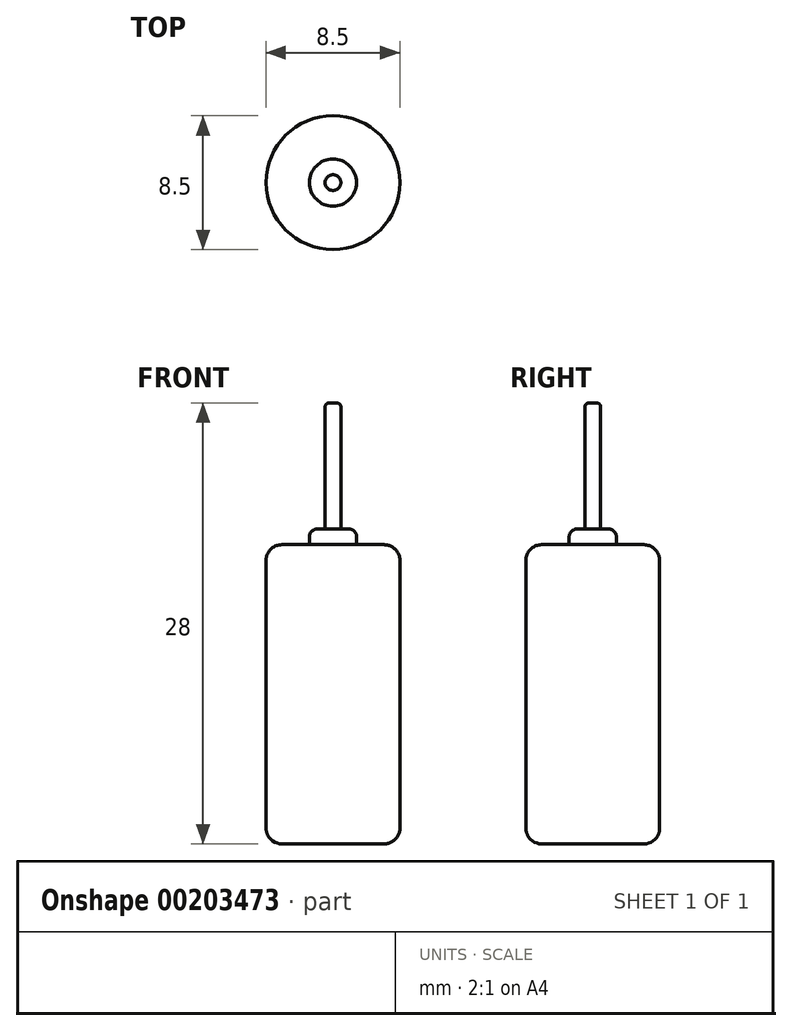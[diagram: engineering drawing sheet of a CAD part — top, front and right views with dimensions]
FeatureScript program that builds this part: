
annotation { "Feature Type Name" : "Feature", "Feature Type Description" : "" }
export const myFeature = defineFeature(function(context is Context, id is Id, definition is map)
    precondition{}
    {
        {
            var Q0;
            Q0=qCreatedBy(makeId("Top.planeOp"),FACE);
            var sketch = newSketch(context, id + "F0", { "sketchPlane" : qUnion([Q0])});
            skCircle(sketch, "E0", {"center": v(0, 0) * mm, "radius": 4.25 * mm});
            skSolve(sketch);
        }
        {
            var Q0;
            Q0=makeQuery(id+"F0.imprint","IMPRINT",FACE,{"disambiguationData":[TD([[makeQuery(id+"F0.imprint","IMPRINT",EDGE,{"derivedFrom":sQuery(id+"F0.wireOp",EDGE,"E0")}),1.0]])]});
            extrude(context, id + "F1", {"entities" : qUnion([Q0]), "depth" : 19 * mm});
        }
        {
            var Q0;
            Q0=makeQuery(id+"F1.opExtrude","CAP_EDGE",EDGE,{"disambiguationData":[OSD([sQuery(id+"F0.wireOp",EDGE,"E0")])],"isStart":false});
            var Q1;
            Q1=makeQuery(id+"F1.opExtrude","CAP_EDGE",EDGE,{"disambiguationData":[OSD([sQuery(id+"F0.wireOp",EDGE,"E0")])],"isStart":true});
            fillet(context, id + "F2", {"entities" : qUnion([Q0, Q1]), "radius" : 1 * mm, "tangentPropagation" : true, "allowEdgeOverflow" : false});
        }
        {
            var Q0;
            Q0=makeQuery(id+"F1.opExtrude","CAP_FACE",FACE,{"disambiguationData":[OSD([sQuery(id+"F0.wireOp",EDGE,"E0")])],"isStart":false});
            var sketch = newSketch(context, id + "F3", { "sketchPlane" : qUnion([Q0])});
            skCircle(sketch, "E1", {"center": v(0, 0) * mm, "radius": 1.5 * mm});
            skSolve(sketch);
        }
        {
            var Q0;
            Q0=makeQuery(id+"F3.imprint","IMPRINT",FACE,{"disambiguationData":[TD([[makeQuery(id+"F3.imprint","IMPRINT",EDGE,{"derivedFrom":sQuery(id+"F3.wireOp",EDGE,"E1")}),1.0]])]});
            extrude(context, id + "F4", {"entities" : qUnion([Q0]), "operationType" : NewBodyOperationType.ADD, "depth" : 1 * mm});
        }
        {
            var Q0;
            Q0=makeQuery(id+"F4.opExtrude","CAP_EDGE",EDGE,{"disambiguationData":[OSD([sQuery(id+"F3.wireOp",EDGE,"E1")])],"isStart":false});
            fillet(context, id + "F5", {"entities" : qUnion([Q0]), "radius" : .5 * mm, "tangentPropagation" : true, "allowEdgeOverflow" : false});
        }
        {
            var Q0;
            Q0=makeQuery(id+"F4.opExtrude","CAP_FACE",FACE,{"disambiguationData":[OSD([sQuery(id+"F3.wireOp",EDGE,"E1")])],"isStart":false});
            var sketch = newSketch(context, id + "F6", { "sketchPlane" : qUnion([Q0])});
            skSolve(sketch);
        }
        {
            var Q0;
            {var subQ0=sQuery(id+"F3.wireOp",EDGE,"E1");Q0=makeQuery(id+"F6.imprint","IMPRINT",FACE,{"disambiguationData":[TD([[makeQuery(id+"F6.imprint","IMPRINT",EDGE,{"derivedFrom":makeQuery(id+"F5.opFillet","BLEND_EDGE",EDGE,{"blendedFrom":[makeQuery(id+"F4.opExtrude","CAP_EDGE",EDGE,{"disambiguationData":[OSD([subQ0])],"isStart":false}),makeQuery(id+"F4.opExtrude","CAP_FACE",FACE,{"disambiguationData":[OSD([subQ0])],"isStart":false})],"blendedInto":[makeQuery(id+"F4.opExtrude","CAP_FACE",FACE,{"disambiguationData":[OSD([subQ0])],"isStart":false})]})}),1.0]])]});}
            var sketch = newSketch(context, id + "F7", { "sketchPlane" : qUnion([Q0])});
            skCircle(sketch, "E2", {"center": v(0, 0) * mm, "radius": 0.5 * mm});
            skSolve(sketch);
        }
        {
            var Q0;
            Q0 = qSketchRegion(id + "F7", true);
            extrude(context, id + "F8", {"entities" : qUnion([Q0]), "operationType" : NewBodyOperationType.ADD, "depth" : 8 * mm});
        }
        {
            var Q0;
            Q0=makeQuery(id+"F8.opExtrude","CAP_EDGE",EDGE,{"disambiguationData":[OSD([sQuery(id+"F7.wireOp",EDGE,"E2")])],"isStart":false});
            fillet(context, id + "F9", {"entities" : qUnion([Q0]), "radius" : .25 * mm, "tangentPropagation" : true, "allowEdgeOverflow" : false});
        }
    });
